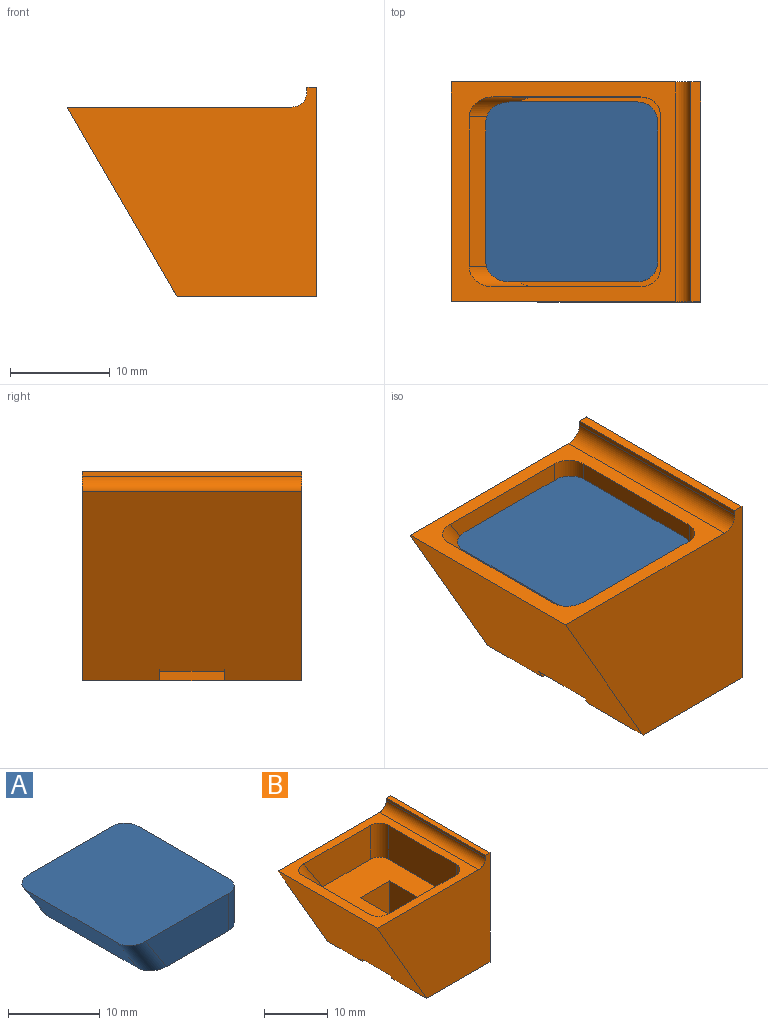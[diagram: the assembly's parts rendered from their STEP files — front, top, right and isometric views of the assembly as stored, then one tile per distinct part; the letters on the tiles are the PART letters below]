
ASSEMBLY  parts=2 mates=1
PART A: 10 faces, bbox 17.2x18x7.2 mm
  f0: plane 18x14mm, normal (0,0,-1), area 248.2mm2, adj f1,f3,f4,f5,f6,f7,f8,f9
  f1: plane 14x5mm, normal (1,0,0), area 70mm2, adj f0,f2,f6,f8
  f2: plane 18x17.21mm, normal (0,0,1), area 306.1mm2, adj f1,f3,f4,f5,f6,f7,f8,f9
  f3: plane 14x5mm, normal (-0.84,0,-0.54), area 83.2mm2, adj f0,f2,f7,f9
  f4: plane 12.84x5mm, normal (0,-1,0), area 56.1mm2, adj f0,f2,f8,f9
  f5: plane 12.84x5mm, normal (0,1,0), area 56.1mm2, adj f0,f2,f6,f7
  f6: cylinder r=2mm len=5mm, axis (0,0,1), area 15.7mm2, adj f0,f1,f2,f5
  f7: cylinder r=2mm len=7.16mm, axis (0.54,0,-0.84), area 18.7mm2, adj f0,f2,f3,f5
  f8: cylinder r=2mm len=5mm, axis (0,0,-1), area 15.7mm2, adj f0,f1,f2,f4
  f9: cylinder r=2mm len=7.16mm, axis (-0.54,0,0.84), area 18.7mm2, adj f0,f2,f3,f4
PART B: 22 faces, bbox 25x22x21 mm
  f0: plane 19x15mm, normal (0,0,1), area 239mm2, adj f9,f10,f11,f12,f14,f15,f16,f17
  f1: plane 22.5x22mm, normal (0,0,1), area 134.4mm2, adj f2,f3,f8,f9,f10,f11,f12,f13
  f2: plane 25x21mm, normal (0,1,0), area 373mm2, adj f1,f4,f5,f6,f7,f8,f13
  f3: plane 25x21mm, normal (0,-1,0), area 373mm2, adj f1,f4,f5,f6,f7,f8,f13
  f4: plane 22x21mm, normal (1,0,0), area 462mm2, adj f2,f3,f5,f7
  f5: plane 22x14mm, normal (0,0,-1), area 269.4mm2, adj f2,f3,f4,f13,f18,f20,f21
  f6: plane 22x0.5mm, normal (-1,0,0), area 11mm2, adj f2,f3,f7,f8
  f7: plane 22x1mm, normal (0,0,1), area 22mm2, adj f2,f3,f4,f6
  f8: cylinder r=1.5mm len=22mm, axis (0,-1,0), area 51.8mm2, adj f1,f2,f3,f6
  f9: plane 14.8x6.5mm, normal (0,-1,0), area 82.6mm2, adj f0,f1,f14,f17
  f10: plane 14.8x6.5mm, normal (0,1,0), area 82.6mm2, adj f0,f1,f15,f16
  f11: plane 15x6.5mm, normal (-1,0,0), area 97.5mm2, adj f0,f1,f16,f17
  f12: plane 15x6.5mm, normal (0.84,0,0.54), area 115.9mm2, adj f0,f1,f14,f15
  f13: plane 22x19mm, normal (-0.87,0,-0.5), area 475.7mm2, adj f1,f2,f3,f5,f18,f19,f20
  f14: cylinder r=2mm len=8.66mm, axis (0.54,0,-0.84), area 24.3mm2, adj f0,f1,f9,f12
  f15: cylinder r=2mm len=8.66mm, axis (0.54,0,-0.84), area 24.3mm2, adj f0,f1,f10,f12
  f16: cylinder r=2mm len=6.5mm, axis (0,0,1), area 20.4mm2, adj f0,f1,f10,f11
  f17: cylinder r=2mm len=6.5mm, axis (0,0,-1), area 20.4mm2, adj f0,f1,f9,f11
  f18: plane 12.5x6.5mm, normal (0,-1,0), area 81mm2, adj f0,f5,f13,f19,f21
  f19: plane 11.53x6.5mm, normal (1,0,0), area 74.9mm2, adj f0,f13,f18,f20
  f20: plane 12.5x6.5mm, normal (0,1,0), area 81mm2, adj f0,f5,f13,f19,f21
  f21: plane 12.5x6.5mm, normal (-1,0,0), area 81.3mm2, adj f0,f5,f18,f20
PLACE A t=(-6.79,-6.59,-8.24)mm
PLACE B t=(-14.97,-15.59,-20.74)mm
MATE fastened B.f0 <-> A.f0  axis (0,0,1) through (-13.78,-15.59,-8.24)mm
